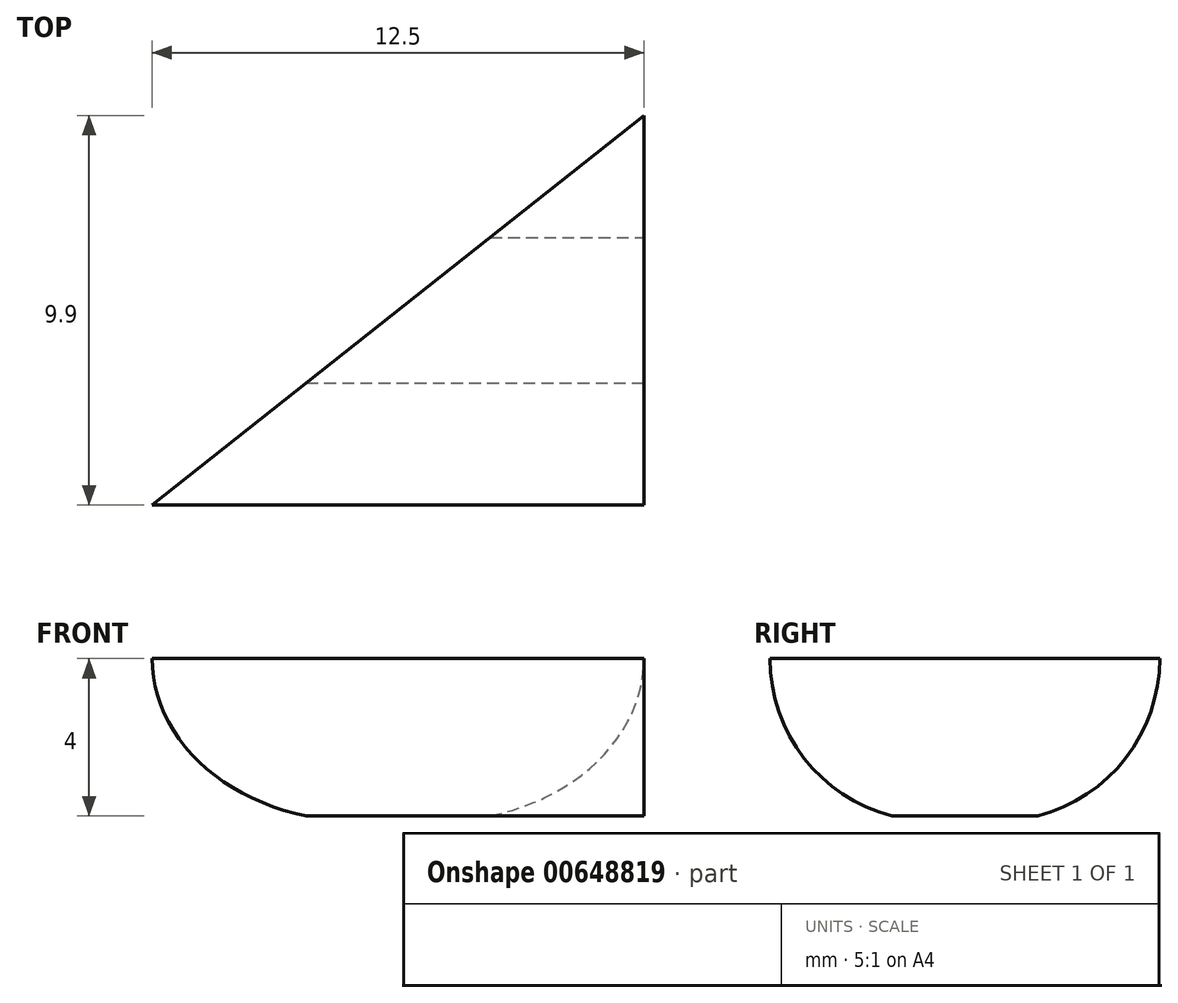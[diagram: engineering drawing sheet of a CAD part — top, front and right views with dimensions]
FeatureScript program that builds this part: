
annotation { "Feature Type Name" : "Feature", "Feature Type Description" : "" }
export const myFeature = defineFeature(function(context is Context, id is Id, definition is map)
    precondition{}
    {
        {
            var Q0;
            Q0=qCreatedBy(makeId("Top.planeOp"),FACE);
            var sketch = newSketch(context, id + "F0", { "sketchPlane" : qUnion([Q0])});
            skLineSegment(sketch, "E0.bottom", {"start": v(2, 4.95) * mm, "end": v(-2, 4.95) * mm});
            skLineSegment(sketch, "E0.top", {"start": v(2, -4.95) * mm, "end": v(-2, -4.95) * mm});
            skLineSegment(sketch, "E0.left", {"start": v(2, 4.95) * mm, "end": v(2, -4.95) * mm});
            skLineSegment(sketch, "E0.right", {"start": v(-2, 4.95) * mm, "end": v(-2, -4.95) * mm});
            skPoint(sketch, "E0.middle", {"position": v(0, 0) * mm});
            skLineSegment(sketch, "E1", {"start": v(2, 4.95) * mm, "end": v(4, 4.95) * mm});
            skLineSegment(sketch, "E2", {"start": v(2, -4.95) * mm, "end": v(4, -4.95) * mm});
            skLineSegment(sketch, "E3", {"start": v(-2, 4.95) * mm, "end": v(-2, 1.85) * mm});
            skLineSegment(sketch, "E4", {"start": v(-2, -4.95) * mm, "end": v(-2, -1.85) * mm});
            skArc(sketch, "E5", {"start": v(2, 4.95) * mm, "mid": v(-0.53, 4.08) * mm, "end": v(-2, 1.85) * mm});
            skArc(sketch, "E6", {"start": v(2, -4.95) * mm, "mid": v(-0.53, -4.08) * mm, "end": v(-2, -1.85) * mm});
            skSolve(sketch);
        }
        {
            var Q0;
            Q0=makeQuery(id+"F0.imprint","IMPRINT",FACE,{"disambiguationData":[TD([[makeQuery(id+"F0.imprint","IMPRINT",EDGE,{"derivedFrom":sQuery(id+"F0.wireOp",EDGE,"E0.left")}),-1.0]])]});
            extrude(context, id + "F1", {"entities" : qUnion([Q0]), "depth" : 12.5 * mm, "offsetDistance" : 25 * mm});
        }
        {
            var Q0;
            Q0=makeQuery(id+"F1.opExtrude","SWEPT_FACE",FACE,{"disambiguationData":[OSD([sQuery(id+"F0.wireOp",EDGE,"E0.left")])]});
            var sketch = newSketch(context, id + "F2", { "sketchPlane" : qUnion([Q0])});
            skPoint(sketch, "E7.0", {"position": v(4.95, 12.5) * mm});
            skPoint(sketch, "E8.0", {"position": v(4.95, 0) * mm});
            skPoint(sketch, "E9.0", {"position": v(-4.95, 0) * mm});
            skPoint(sketch, "E10.0", {"position": v(-4.95, 12.5) * mm});
            skLineSegment(sketch, "E11", {"start": v(-4.95, 0) * mm, "end": v(4.95, 12.5) * mm});
            skLineSegment(sketch, "E12", {"start": v(-4.95, 12.5) * mm, "end": v(4.95, 0) * mm});
            skCircle(sketch, "E13", {"center": v(0, 6.25) * mm, "radius": 2.3 * mm});
            skSolve(sketch);
        }
        {
            var Q0;
            {var subQ0=sQuery(id+"F2.wireOp",EDGE,"E13");var subQ1=sQuery(id+"F2.wireOp",EDGE,"E11");var subQ2=makeQuery(id+"F2.imprint","INTERSECT",VERTEX,{"disambiguationData":[OD(0.0)],"derivedFrom":[subQ1,subQ0]});Q0=makeQuery(id+"F2.imprint","IMPRINT",FACE,{"disambiguationData":[TD([[makeQuery(id+"F2.imprint","IMPRINT",EDGE,{"disambiguationData":[TD([[subQ2,-1.0]])],"derivedFrom":subQ1}),-1.0]])]});}
            var Q1;
            {var subQ0=sQuery(id+"F2.wireOp",EDGE,"E12");var subQ1=sQuery(id+"F2.wireOp",EDGE,"E11");var subQ2=makeQuery(id+"F2.imprint","INTERSECT",VERTEX,{"derivedFrom":[subQ1,subQ0]});Q1=makeQuery(id+"F2.imprint","IMPRINT",FACE,{"disambiguationData":[TD([[makeQuery(id+"F2.imprint","IMPRINT",EDGE,{"disambiguationData":[TD([[subQ2,-1.0]])],"derivedFrom":subQ1}),-1.0]])]});}
            var Q2;
            {var subQ0=sQuery(id+"F2.wireOp",EDGE,"E12");var subQ1=sQuery(id+"F2.wireOp",EDGE,"E11");var subQ2=makeQuery(id+"F2.imprint","INTERSECT",VERTEX,{"derivedFrom":[subQ1,subQ0]});Q2=makeQuery(id+"F2.imprint","IMPRINT",FACE,{"disambiguationData":[TD([[makeQuery(id+"F2.imprint","IMPRINT",EDGE,{"disambiguationData":[TD([[subQ2,-1.0]])],"derivedFrom":subQ1}),1.0]])]});}
            var Q3;
            {var subQ0=sQuery(id+"F2.wireOp",EDGE,"E13");var subQ1=sQuery(id+"F2.wireOp",EDGE,"E11");var subQ2=makeQuery(id+"F2.imprint","INTERSECT",VERTEX,{"disambiguationData":[OD(0.0)],"derivedFrom":[subQ1,subQ0]});Q3=makeQuery(id+"F2.imprint","IMPRINT",FACE,{"disambiguationData":[TD([[makeQuery(id+"F2.imprint","IMPRINT",EDGE,{"disambiguationData":[TD([[subQ2,-1.0]])],"derivedFrom":subQ1}),1.0]])]});}
            extrude(context, id + "F3", {"entities" : qUnion([Q0, Q1, Q2, Q3]), "operationType" : NewBodyOperationType.REMOVE, "oppositeDirection" : true, "depth" : 4 * mm, "offsetDistance" : 25 * mm});
        }
        {
            var Q0;
            Q0=makeQuery(id+"F1.opExtrude","SWEPT_BODY",BODY,{"disambiguationData":[OSD([sQuery(id+"F0.wireOp",EDGE,"E0.left"),sQuery(id+"F0.wireOp",EDGE,"E0.right"),sQuery(id+"F0.wireOp",EDGE,"E5"),sQuery(id+"F0.wireOp",EDGE,"E6")])]});
            var Q1;
            Q1=makeQuery(id+"F1.opExtrude","CAP_EDGE",EDGE,{"disambiguationData":[OSD([sQuery(id+"F0.wireOp",EDGE,"E0.left")])],"isStart":true});
            transform(context, id + "F4", {"entities" : qUnion([Q0]), "transformType" : TransformType.ROTATION, "transformAxis" : qUnion([Q1]), "angle" : 90 * degree, "makeCopy" : false});
        }
    });
